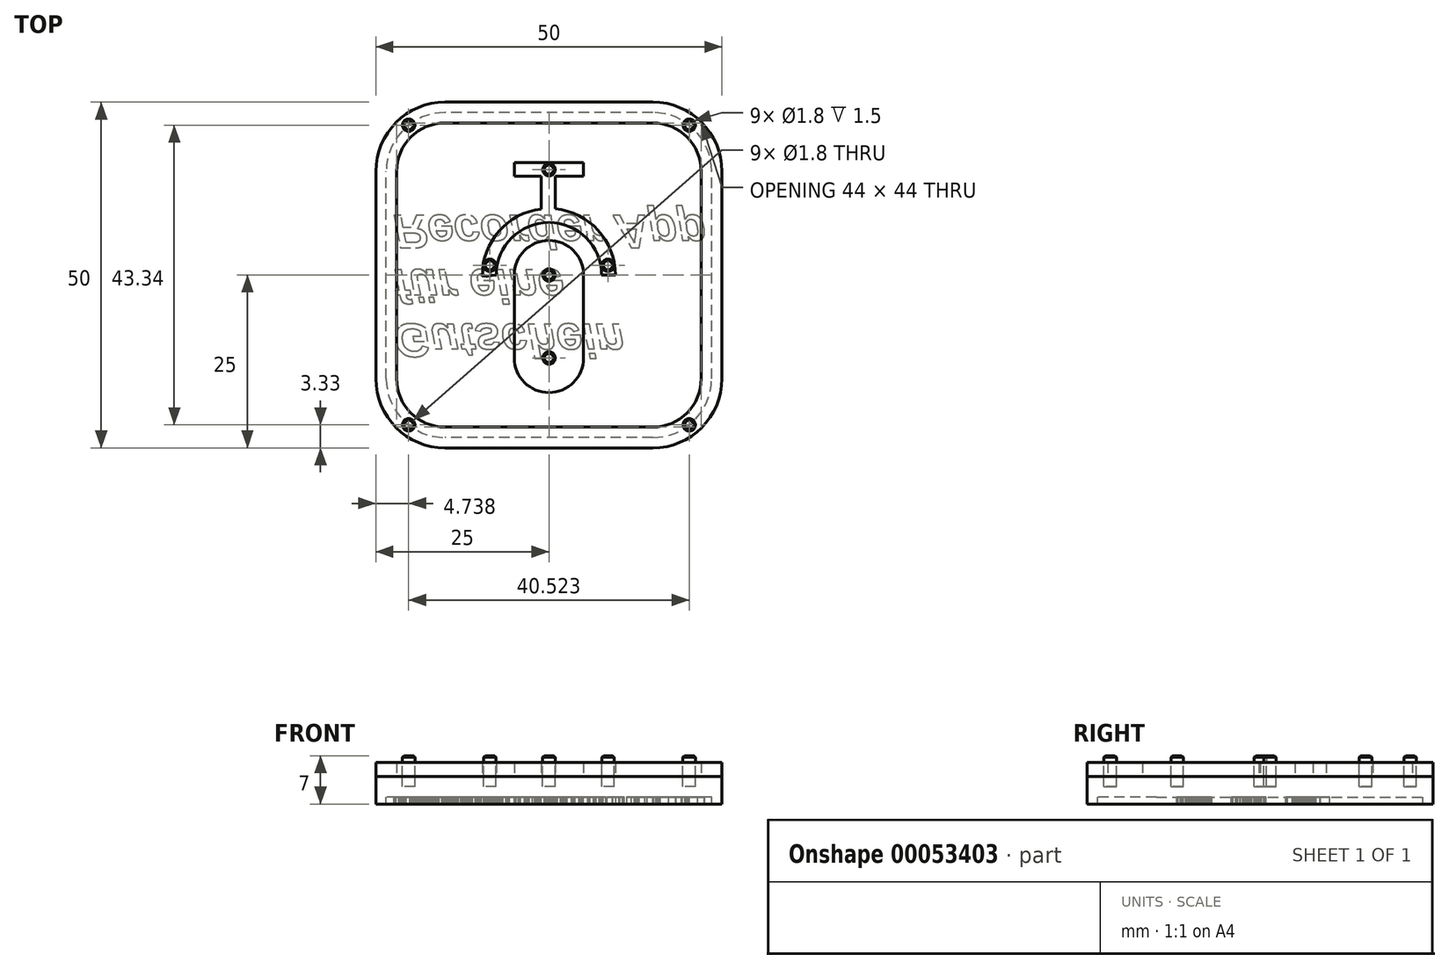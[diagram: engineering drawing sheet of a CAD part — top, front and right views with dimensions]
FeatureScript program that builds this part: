
annotation { "Feature Type Name" : "Feature", "Feature Type Description" : "" }
export const myFeature = defineFeature(function(context is Context, id is Id, definition is map)
    precondition{}
    {
        {
            var Q0;
            Q0=qCreatedBy(makeId("Top.planeOp"),FACE);
            var sketch = newSketch(context, id + "F0", { "sketchPlane" : qUnion([Q0])});
            skLineSegment(sketch, "E0.rect.bottom", {"start": v(25, -25) * mm, "end": v(-25, -25) * mm});
            skLineSegment(sketch, "E0.rect.top", {"start": v(25, 25) * mm, "end": v(-25, 25) * mm});
            skLineSegment(sketch, "E0.rect.left", {"start": v(25, -25) * mm, "end": v(25, 25) * mm});
            skLineSegment(sketch, "E0.rect.right", {"start": v(-25, -25) * mm, "end": v(-25, 25) * mm});
            skPoint(sketch, "E0.rect.middle", {"position": v(0, 0) * mm});
            skSolve(sketch);
        }
        {
            var Q0;
            Q0=makeQuery(id+"F0.imprint","IMPRINT",FACE,{"disambiguationData":[TD([[makeQuery(id+"F0.imprint","IMPRINT",EDGE,{"derivedFrom":sQuery(id+"F0.wireOp",EDGE,"E0.rect.bottom")}),-1.0]])]});
            extrude(context, id + "F1", {"entities" : qUnion([Q0]), "depth" : 3 * mm});
        }
        {
            var Q0;
            Q0=makeQuery(id+"F1.opExtrude","SWEPT_EDGE",EDGE,{"disambiguationData":[OSD([sQuery(id+"F0.wireOp",EDGE,"E0.rect.bottom"),sQuery(id+"F0.wireOp",EDGE,"E0.rect.left")])]});
            var Q1;
            Q1=makeQuery(id+"F1.opExtrude","SWEPT_EDGE",EDGE,{"disambiguationData":[OSD([sQuery(id+"F0.wireOp",EDGE,"E0.rect.top"),sQuery(id+"F0.wireOp",EDGE,"E0.rect.left")])]});
            var Q2;
            Q2=makeQuery(id+"F1.opExtrude","SWEPT_EDGE",EDGE,{"disambiguationData":[OSD([sQuery(id+"F0.wireOp",EDGE,"E0.rect.top"),sQuery(id+"F0.wireOp",EDGE,"E0.rect.right")])]});
            var Q3;
            Q3=makeQuery(id+"F1.opExtrude","SWEPT_EDGE",EDGE,{"disambiguationData":[OSD([sQuery(id+"F0.wireOp",EDGE,"E0.rect.bottom"),sQuery(id+"F0.wireOp",EDGE,"E0.rect.right")])]});
            fillet(context, id + "F2", {"entities" : qUnion([Q0, Q1, Q2, Q3]), "radius" : 10 * mm, "tangentPropagation" : true, "allowEdgeOverflow" : false});
        }
        {
            var Q0;
            Q0=makeQuery(id+"F1.opExtrude","CAP_FACE",FACE,{"disambiguationData":[OSD([sQuery(id+"F0.wireOp",EDGE,"E0.rect.bottom"),sQuery(id+"F0.wireOp",EDGE,"E0.rect.top"),sQuery(id+"F0.wireOp",EDGE,"E0.rect.left"),sQuery(id+"F0.wireOp",EDGE,"E0.rect.right")])],"isStart":false});
            var sketch = newSketch(context, id + "F3", { "sketchPlane" : qUnion([Q0])});
            skArc(sketch, "E1.0", {"start": v(-22, -15) * mm, "mid": v(-19.95, -19.95) * mm, "end": v(-15, -22) * mm});
            skLineSegment(sketch, "E1.1", {"start": v(-22, 15) * mm, "end": v(-22, -15) * mm});
            skLineSegment(sketch, "E1.2", {"start": v(-15, -22) * mm, "end": v(15, -22) * mm});
            skArc(sketch, "E1.3", {"start": v(-15, 22) * mm, "mid": v(-19.95, 19.95) * mm, "end": v(-22, 15) * mm});
            skArc(sketch, "E1.4", {"start": v(15, -22) * mm, "mid": v(19.95, -19.95) * mm, "end": v(22, -15) * mm});
            skLineSegment(sketch, "E1.5", {"start": v(22, -15) * mm, "end": v(22, 15) * mm});
            skArc(sketch, "E1.6", {"start": v(22, 15) * mm, "mid": v(19.95, 19.95) * mm, "end": v(15, 22) * mm});
            skLineSegment(sketch, "E1.7", {"start": v(15, 22) * mm, "end": v(-15, 22) * mm});
            skSolve(sketch);
        }
        {
            var Q0;
            Q0=makeQuery(id+"F3.imprint","IMPRINT",FACE,{"disambiguationData":[TD([[makeQuery(id+"F3.imprint","IMPRINT",EDGE,{"derivedFrom":sQuery(id+"F3.wireOp",EDGE,"E1.0")}),-1.0]])]});
            extrude(context, id + "F4", {"entities" : qUnion([Q0]), "depth" : 2 * mm});
        }
        {
            var Q0;
            Q0=makeQuery(id+"F1.opExtrude","CAP_FACE",FACE,{"disambiguationData":[OSD([sQuery(id+"F0.wireOp",EDGE,"E0.rect.bottom"),sQuery(id+"F0.wireOp",EDGE,"E0.rect.top"),sQuery(id+"F0.wireOp",EDGE,"E0.rect.left"),sQuery(id+"F0.wireOp",EDGE,"E0.rect.right")])],"isStart":false});
            var sketch = newSketch(context, id + "F5", { "sketchPlane" : qUnion([Q0])});
            skCircle(sketch, "E2", {"center": v(0, 12) * mm, "radius": 5 * mm});
            skCircle(sketch, "E3", {"center": v(0, 0) * mm, "radius": 5 * mm});
            skLineSegment(sketch, "E4", {"start": v(-5, 12) * mm, "end": v(-5, 0) * mm});
            skLineSegment(sketch, "E5", {"start": v(5, 12) * mm, "end": v(5, 0) * mm});
            skArc(sketch, "E6", {"start": v(7.6, 0) * mm, "mid": v(0, -7.6) * mm, "end": v(-7.6, 0) * mm});
            skArc(sketch, "E7.0", {"start": v(9.6, 0.19) * mm, "mid": v(0.1, -9.6) * mm, "end": v(-9.6, 0) * mm});
            skLineSegment(sketch, "E8", {"start": v(-7.6, 0) * mm, "end": v(-9.6, 0) * mm});
            skLineSegment(sketch, "E9", {"start": v(7.6, 0) * mm, "end": v(9.6, 0.19) * mm});
            skLineSegment(sketch, "E10.rect.bottom", {"start": v(1.1, -16.26) * mm, "end": v(-0.9, -16.26) * mm});
            skLineSegment(sketch, "E10.rect.top", {"start": v(1.1, -9.04) * mm, "end": v(-0.9, -9.04) * mm});
            skLineSegment(sketch, "E10.rect.left", {"start": v(1.1, -16.26) * mm, "end": v(1.1, -9.04) * mm});
            skLineSegment(sketch, "E10.rect.right", {"start": v(-0.9, -16.26) * mm, "end": v(-0.9, -9.04) * mm});
            skPoint(sketch, "E10.rect.middle", {"position": v(0.1, -12.65) * mm});
            skPoint(sketch, "E10.rect.middle.positionSnap0", {"position": v(0.1, -9.6) * mm});
            skPoint(sketch, "E10.rect.centerSnap0", {"position": v(0.1, -9.6) * mm});
            skLineSegment(sketch, "E11.rect.bottom", {"start": v(4.95, -16.26) * mm, "end": v(-4.95, -16.26) * mm});
            skLineSegment(sketch, "E11.rect.top", {"start": v(4.95, -14.26) * mm, "end": v(-4.95, -14.26) * mm});
            skLineSegment(sketch, "E11.rect.left", {"start": v(4.95, -16.26) * mm, "end": v(4.95, -14.26) * mm});
            skLineSegment(sketch, "E11.rect.right", {"start": v(-4.95, -16.26) * mm, "end": v(-4.95, -14.26) * mm});
            skPoint(sketch, "E11.rect.middle", {"position": v(0, -15.26) * mm});
            skSolve(sketch);
        }
        {
            var Q0;
            Q0 = qSketchRegion(id + "F5", true);
            extrude(context, id + "F6", {"entities" : qUnion([Q0]), "depth" : 2 * mm});
        }
        {
            var Q0;
            Q0=makeQuery(id+"F1.opExtrude","CAP_FACE",FACE,{"disambiguationData":[OSD([sQuery(id+"F0.wireOp",EDGE,"E0.rect.bottom"),sQuery(id+"F0.wireOp",EDGE,"E0.rect.top"),sQuery(id+"F0.wireOp",EDGE,"E0.rect.left"),sQuery(id+"F0.wireOp",EDGE,"E0.rect.right")])],"isStart":true});
            var sketch = newSketch(context, id + "F7", { "sketchPlane" : qUnion([Q0])});
            skText(sketch, "E12", { "text": "Gutschein\nfür eine\nRecorder App", "fontName": "Arimo-BoldItalic.ttf"});
            const initialGuessF7  = {"E12": [-0.0225, 0.00708, 1, 0, 0.00492]};
            skSetInitialGuess(sketch, initialGuessF7);
            skSolve(sketch);
        }
        {
            var Q0;
            Q0 = qSketchRegion(id + "F7", true);
            extrude(context, id + "F8", {"entities" : qUnion([Q0]), "operationType" : NewBodyOperationType.ADD, "depth" : 1 * mm});
        }
        {
            var Q0;
            Q0=qCreatedBy(makeId("Front.planeOp"),FACE);
            var sketch = newSketch(context, id + "F9", { "sketchPlane" : qUnion([Q0])});
            skLineSegment(sketch, "E13", {"start": v(0, 12.8) * mm, "end": v(0, -9.27) * mm, "construction": true});
            skSolve(sketch);
        }
        {
            var Q0;
            Q0=makeQuery(id+"F6.opExtrude","SWEPT_BODY",BODY,{"disambiguationData":[OSD([sQuery(id+"F5.wireOp",EDGE,"E2"),sQuery(id+"F5.wireOp",EDGE,"E3"),sQuery(id+"F5.wireOp",EDGE,"E4"),sQuery(id+"F5.wireOp",EDGE,"E5")])]});
            var Q1;
            Q1=makeQuery(id+"F6.opExtrude","SWEPT_BODY",BODY,{"disambiguationData":[OSD([sQuery(id+"F5.wireOp",EDGE,"E6"),sQuery(id+"F5.wireOp",EDGE,"E7.0"),sQuery(id+"F5.wireOp",EDGE,"E8"),sQuery(id+"F5.wireOp",EDGE,"E9"),sQuery(id+"F5.wireOp",EDGE,"E10.rect.left"),sQuery(id+"F5.wireOp",EDGE,"E10.rect.right"),sQuery(id+"F5.wireOp",EDGE,"E11.rect.bottom"),sQuery(id+"F5.wireOp",EDGE,"E11.rect.top"),sQuery(id+"F5.wireOp",EDGE,"E11.rect.left"),sQuery(id+"F5.wireOp",EDGE,"E11.rect.right")])]});
            var Q2;
            Q2=sQuery(id+"F9.wireOp",EDGE,"E13");
            transform(context, id + "F10", {"entities" : qUnion([Q0, Q1]), "transformType" : TransformType.ROTATION, "transformAxis" : qUnion([Q2]), "angle" : 180 * degree, "makeCopy" : false});
        }
        {
            var Q0;
            Q0=makeQuery(id+"F6.opExtrude","CAP_FACE",FACE,{"disambiguationData":[OSD([sQuery(id+"F5.wireOp",EDGE,"E2"),sQuery(id+"F5.wireOp",EDGE,"E3"),sQuery(id+"F5.wireOp",EDGE,"E4"),sQuery(id+"F5.wireOp",EDGE,"E5")])],"isStart":false});
            var sketch = newSketch(context, id + "F11", { "sketchPlane" : qUnion([Q0])});
            skCircle(sketch, "E14", {"center": v(0, 0) * mm, "radius": 0.9 * mm});
            skCircle(sketch, "E15", {"center": v(0, -12) * mm, "radius": 0.9 * mm});
            skCircle(sketch, "E16", {"center": v(0, 15.23) * mm, "radius": 0.9 * mm});
            skCircle(sketch, "E17", {"center": v(8.53, 1.4) * mm, "radius": 0.9 * mm});
            skCircle(sketch, "E18.1.1.0", {"center": v(20.26, -21.67) * mm, "radius": 0.9 * mm});
            skLineSegment(sketch, "E19", {"start": v(0, 15.23) * mm, "end": v(0, 0) * mm, "construction": true});
            skCircle(sketch, "E20.MirrorC", {"center": v(-20.26, -21.67) * mm, "radius": 0.9 * mm});
            skLineSegment(sketch, "E21", {"start": v(-26.91, 0) * mm, "end": v(32.26, 0) * mm, "construction": true});
            skCircle(sketch, "E22.MirrorC", {"center": v(20.26, 21.67) * mm, "radius": 0.9 * mm});
            skCircle(sketch, "E23.MirrorC", {"center": v(-20.26, 21.67) * mm, "radius": 0.9 * mm});
            skCircle(sketch, "E24.MirrorC", {"center": v(-8.53, 1.4) * mm, "radius": 0.9 * mm});
            skSolve(sketch);
        }
        {
            var Q0;
            Q0 = qSketchRegion(id + "F11", true);
            extrude(context, id + "F12", {"entities" : qUnion([Q0]), "operationType" : NewBodyOperationType.ADD, "depth" : 1 * mm});
        }
        {
            var Q0;
            Q0 = qSketchRegion(id + "F11", true);
            extrude(context, id + "F13", {"entities" : qUnion([Q0]), "operationType" : NewBodyOperationType.REMOVE, "oppositeDirection" : true, "depth" : 3.5 * mm});
        }
        {
            var Q0;
            Q0=makeQuery(id+"F12.opExtrude","CAP_EDGE",EDGE,{"disambiguationData":[OSD([sQuery(id+"F11.wireOp",EDGE,"E15")])],"isStart":false});
            var Q1;
            Q1=makeQuery(id+"F12.opExtrude","CAP_EDGE",EDGE,{"disambiguationData":[OSD([sQuery(id+"F11.wireOp",EDGE,"E14")])],"isStart":false});
            var Q2;
            Q2=makeQuery(id+"F12.opExtrude","CAP_EDGE",EDGE,{"disambiguationData":[OSD([sQuery(id+"F11.wireOp",EDGE,"2d3db073-8b09-40e7-92af-3565a8c03be5")])],"isStart":false});
            var Q3;
            Q3=makeQuery(id+"F12.opExtrude","CAP_EDGE",EDGE,{"disambiguationData":[OSD([sQuery(id+"F11.wireOp",EDGE,"E17")])],"isStart":false});
            var Q4;
            Q4=makeQuery(id+"F12.opExtrude","CAP_EDGE",EDGE,{"disambiguationData":[OSD([sQuery(id+"F11.wireOp",EDGE,"E16")])],"isStart":false});
            var Q5;
            Q5=makeQuery(id+"F12.opExtrude","CAP_EDGE",EDGE,{"disambiguationData":[OSD([sQuery(id+"F11.wireOp",EDGE,"82fd7a58-61fe-4f45-9ca0-20dd5d0306a1")])],"isStart":false});
            var Q6;
            Q6=makeQuery(id+"F12.opExtrude","CAP_EDGE",EDGE,{"disambiguationData":[OSD([sQuery(id+"F11.wireOp",EDGE,"E18.1.0.0")])],"isStart":false});
            var Q7;
            Q7=makeQuery(id+"F12.opExtrude","CAP_EDGE",EDGE,{"disambiguationData":[OSD([sQuery(id+"F11.wireOp",EDGE,"E18.1.1.0")])],"isStart":false});
            var Q8;
            Q8=makeQuery(id+"F12.opExtrude","CAP_EDGE",EDGE,{"disambiguationData":[OSD([sQuery(id+"F11.wireOp",EDGE,"E18.0.1.0")])],"isStart":false});
            var Q9;
            Q9=makeQuery(id+"F12.opExtrude","CAP_EDGE",EDGE,{"disambiguationData":[OSD([sQuery(id+"F11.wireOp",EDGE,"E23.MirrorC")])],"isStart":false});
            var Q10;
            Q10=makeQuery(id+"F12.opExtrude","CAP_EDGE",EDGE,{"disambiguationData":[OSD([sQuery(id+"F11.wireOp",EDGE,"E22.MirrorC")])],"isStart":false});
            var Q11;
            Q11=makeQuery(id+"F12.opExtrude","CAP_EDGE",EDGE,{"disambiguationData":[OSD([sQuery(id+"F11.wireOp",EDGE,"E20.MirrorC")])],"isStart":false});
            var Q12;
            Q12=makeQuery(id+"F12.opExtrude","CAP_EDGE",EDGE,{"disambiguationData":[OSD([sQuery(id+"F11.wireOp",EDGE,"E24.MirrorC")])],"isStart":false});
            chamfer(context, id + "F14", {"entities" : qUnion([Q0, Q1, Q2, Q3, Q4, Q5, Q6, Q7, Q8, Q9, Q10, Q11, Q12]), "width" : 0.25 * mm, "tangentPropagation" : true});
        }
        {
            var Q0;
            {var subQ0=sQuery(id+"F0.wireOp",EDGE,"E0.rect.left");var subQ1=sQuery(id+"F0.wireOp",EDGE,"E0.rect.bottom");var subQ2=sQuery(id+"F0.wireOp",EDGE,"E0.rect.right");var subQ3=sQuery(id+"F0.wireOp",EDGE,"E0.rect.top");Q0=makeQuery(id+"F8.boolean.opBoolean","SPLIT",FACE,{"disambiguationData":[TD([makeQuery(id+"F1.opExtrude","SWEPT_FACE",FACE,{"disambiguationData":[OSD([subQ1])]})])],"derivedFrom":makeQuery(id+"F1.opExtrude","CAP_FACE",FACE,{"disambiguationData":[OSD([subQ1,subQ3,subQ0,subQ2])],"isStart":true})});}
            var sketch = newSketch(context, id + "F15", { "sketchPlane" : qUnion([Q0])});
            skPoint(sketch, "E25.1.internal.snap0", {"position": v(0, 25) * mm});
            skLineSegment(sketch, "E26", {"start": v(-31.95, -0.23) * mm, "end": v(35.2, 0.09) * mm, "construction": true});
            skArc(sketch, "E27.0", {"start": v(23.5, 15) * mm, "mid": v(21.01, 21.01) * mm, "end": v(15, 23.5) * mm});
            skLineSegment(sketch, "E27.1", {"start": v(23.5, 15) * mm, "end": v(23.5, -15) * mm});
            skLineSegment(sketch, "E27.2", {"start": v(15, 23.5) * mm, "end": v(-15, 23.5) * mm});
            skArc(sketch, "E27.3", {"start": v(15, -23.5) * mm, "mid": v(21.01, -21.01) * mm, "end": v(23.5, -15) * mm});
            skArc(sketch, "E27.4", {"start": v(-15, 23.5) * mm, "mid": v(-21.01, 21.01) * mm, "end": v(-23.5, 15) * mm});
            skLineSegment(sketch, "E27.5", {"start": v(-23.5, 15) * mm, "end": v(-23.5, -15) * mm});
            skArc(sketch, "E27.6", {"start": v(-23.5, -15) * mm, "mid": v(-21.01, -21.01) * mm, "end": v(-15, -23.5) * mm});
            skLineSegment(sketch, "E27.7", {"start": v(15, -23.5) * mm, "end": v(-15, -23.5) * mm});
            skSolve(sketch);
        }
        {
            var Q0;
            Q0=makeQuery(id+"F15.imprint","IMPRINT",FACE,{"disambiguationData":[TD([[makeQuery(id+"F15.imprint","IMPRINT",EDGE,{"derivedFrom":sQuery(id+"F15.wireOp",EDGE,"E27.0")}),-1.0]])]});
            extrude(context, id + "F16", {"entities" : qUnion([Q0]), "operationType" : NewBodyOperationType.ADD, "depth" : 1 * mm});
        }
    });
